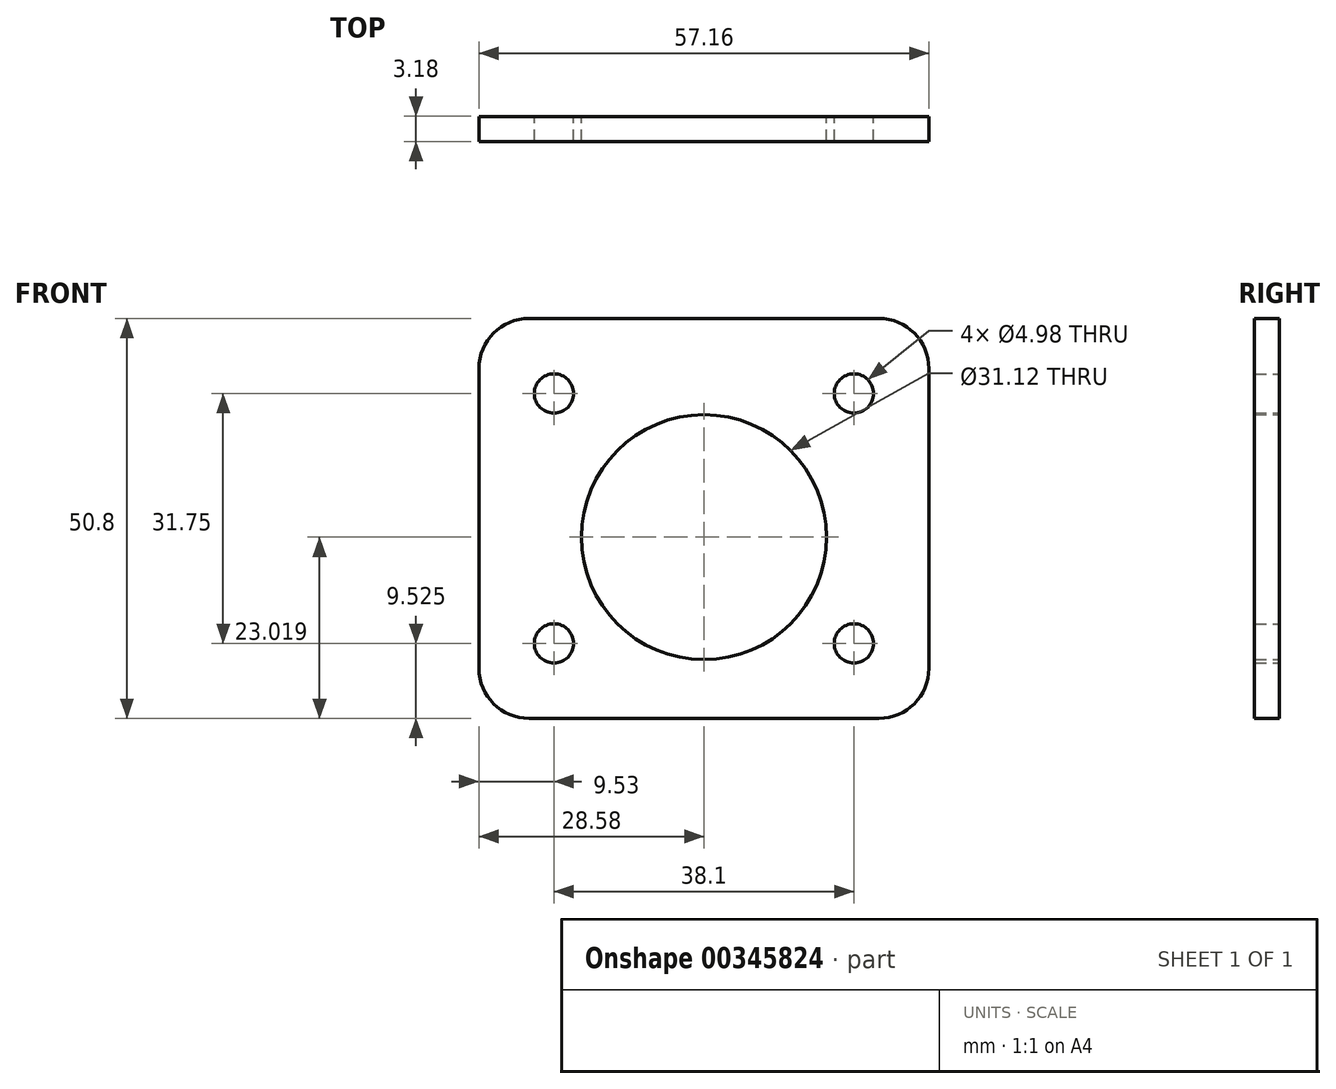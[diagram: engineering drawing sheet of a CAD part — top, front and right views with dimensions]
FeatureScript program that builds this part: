
annotation { "Feature Type Name" : "Feature", "Feature Type Description" : "" }
export const myFeature = defineFeature(function(context is Context, id is Id, definition is map)
    precondition{}
    {
        {
            var Q0;
            Q0=qCreatedBy(makeId("Front.planeOp"),FACE);
            var sketch = newSketch(context, id + "F0", { "sketchPlane" : qUnion([Q0])});
            skLineSegment(sketch, "E0.bottom", {"start": v(-28.58, 25.4) * mm, "end": v(28.58, 25.4) * mm});
            skLineSegment(sketch, "E0.top", {"start": v(-28.58, -25.4) * mm, "end": v(28.58, -25.4) * mm});
            skLineSegment(sketch, "E0.left", {"start": v(-28.58, 25.4) * mm, "end": v(-28.58, -25.4) * mm});
            skLineSegment(sketch, "E0.right", {"start": v(28.58, 25.4) * mm, "end": v(28.58, -25.4) * mm});
            skPoint(sketch, "E0.middle", {"position": v(0, 0) * mm});
            skLineSegment(sketch, "E1.bottom", {"start": v(-19.05, 15.88) * mm, "end": v(19.05, 15.88) * mm, "construction": true});
            skLineSegment(sketch, "E1.top", {"start": v(-19.05, -15.88) * mm, "end": v(19.05, -15.88) * mm, "construction": true});
            skLineSegment(sketch, "E1.left", {"start": v(-19.05, 15.88) * mm, "end": v(-19.05, -15.88) * mm, "construction": true});
            skLineSegment(sketch, "E1.right", {"start": v(19.05, 15.88) * mm, "end": v(19.05, -15.88) * mm, "construction": true});
            skCircle(sketch, "E2", {"center": v(0, -2.38) * mm, "radius": 15.56 * mm});
            skCircle(sketch, "E3", {"center": v(-19.05, 15.88) * mm, "radius": 2.49 * mm});
            skCircle(sketch, "E4", {"center": v(-19.05, -15.88) * mm, "radius": 2.49 * mm});
            skCircle(sketch, "E5", {"center": v(19.05, -15.88) * mm, "radius": 2.49 * mm});
            skCircle(sketch, "E6", {"center": v(19.05, 15.88) * mm, "radius": 2.49 * mm});
            skSolve(sketch);
        }
        {
            var Q0;
            Q0 = qSketchRegion(id + "F0", true);
            extrude(context, id + "F1", {"entities" : qUnion([Q0]), "endBound" : BoundingType.SYMMETRIC, "depth" : 3.17 * mm});
        }
        {
            var Q0;
            Q0=makeQuery(id+"F1.opExtrude","SWEPT_EDGE",EDGE,{"disambiguationData":[OSD([sQuery(id+"F0.wireOp",EDGE,"E0.bottom"),sQuery(id+"F0.wireOp",EDGE,"E0.left")])]});
            var Q1;
            Q1=makeQuery(id+"F1.opExtrude","SWEPT_EDGE",EDGE,{"disambiguationData":[OSD([sQuery(id+"F0.wireOp",EDGE,"E0.bottom"),sQuery(id+"F0.wireOp",EDGE,"E0.right")])]});
            var Q2;
            Q2=makeQuery(id+"F1.opExtrude","SWEPT_EDGE",EDGE,{"disambiguationData":[OSD([sQuery(id+"F0.wireOp",EDGE,"E0.top"),sQuery(id+"F0.wireOp",EDGE,"E0.right")])]});
            var Q3;
            Q3=makeQuery(id+"F1.opExtrude","SWEPT_EDGE",EDGE,{"disambiguationData":[OSD([sQuery(id+"F0.wireOp",EDGE,"E0.top"),sQuery(id+"F0.wireOp",EDGE,"E0.left")])]});
            fillet(context, id + "F2", {"entities" : qUnion([Q0, Q1, Q2, Q3]), "radius" : 6.35 * mm, "tangentPropagation" : true, "allowEdgeOverflow" : false});
        }
    });
